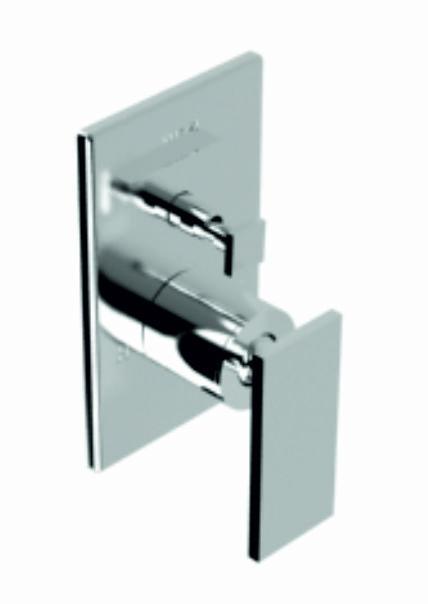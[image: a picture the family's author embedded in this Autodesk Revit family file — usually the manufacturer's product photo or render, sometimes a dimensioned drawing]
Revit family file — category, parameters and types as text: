
# Revit family: Monomando de Regadera E-713
name_source: partatom
category: Plumbing Fixtures
revit_build: Autodesk Revit 2015 (Build: 20140223_1515(x64)
units: mm (PartAtom-declared; Revit-internal decimal feet)

## types (1)
- E-713
    Altura = 7"
    Ancho = 4"
    Brass Chromed = Brass
    Cartucho = Cartucho monomando cerámico Ø40mm
    Default Elevation = 1"
    Description = Monomando para Regadera con Desviador.
    Garantía = El producto HELVEX está garantizado como libre de defectos en materiales y procesos de fabricación. El producto HELVEX está garantizado, en lo que se refiere a los acabados; por un periodo de 10 años en los acabados cromo y duravex, y por 2 años en cabados diferentes al cromo, a partir de la fecha de compra indicada en la factura.
    Instalación = ½" - 14 NPT
    Manufacturer = HELVEX S.A. DE C.V.
    Model = E-713
    Operación = Para abrir el flujo de agua levante la palanca maneral y gire para regular la temperatura.
    Presión máxima de trabajo = 85.3 psi
    Presión mínima de trabajo = 14.2 psi
    Profundidad = 3"
    Satin = Satín
    Type Comments = Monomando Máxima
    Type Image = E-713.jpg

## geometry (parser evidence)
native form markers: Sweep x3
no freeform markers — native parametric forms only
